# Revit family: QF_ELECTROLUXPROFESSIONAL_1LSPHR_TD6-45SLD_G
name_source: partatom
category: Attrezzature speciali
units: mm (PartAtom-declared; Revit-internal decimal feet)

## family parameters
Basato su piano di lavoro = No
Condiviso = No
Punto di calcolo locali = No
Quota connettore circolare = Usa diametro
Sempre verticale = Sì
Taglio con vuoti quando caricato = No
Tipo di parte = Normale

## types (3) — shared parameters
ALL_MODEL_IMAGE = <Nessuno>
Cold Water Size = 0 mm
Compressed Air Pressure = 0.0 Pa
Compressed Air Size = 0 mm
Compressed Air Volume = 0.0 L/s
Condensate Return Size = 0 mm
Cycle = 50 Hz
Depth Actual = 1300 mm  [stored 4.26509 ft]
Descrizione = TUMBLE DRYER DRUM VOLUME 900L CAPACITY 45KG/100LB SLIDING DOOR
Direct Waste Size = 0 mm
Gas Size = 0 mm
Height Actual = 2465 mm  [stored 8.08727 ft]
Hot Water Size = 0 mm
Length Actual = 1314 mm  [stored 4.31102 ft]
Phase = 3
Produttore = Electrolux Professional
Steam Supply Maximum Pressure = 0.0 Pa
Steam Supply Minimum Pressure = 0.0 Pa
Steam Supply Size = 0 mm
URL = https://www.electroluxprofessional.com
Volts = 380 V
Weight in Pounds = 494
zero-valued in all types: Gas KW, Prospetto di default, Steam Pounds per Hour

## per-type parameters (varying)
| type | Item Number | Watts |
| 1L0HAP | 9875030028 | 3 W |
| 1L82B9 | 9875030012 | 2 W |
| 1LT65E | 9875030039 | 3 W |

note: [stored X ft] marks values corroborated as IEEE doubles in the binary element streams (Revit-internal decimal feet)

## geometry (parser evidence)
native form markers: Blend x2, Sweep x2
no freeform markers — native parametric forms only
